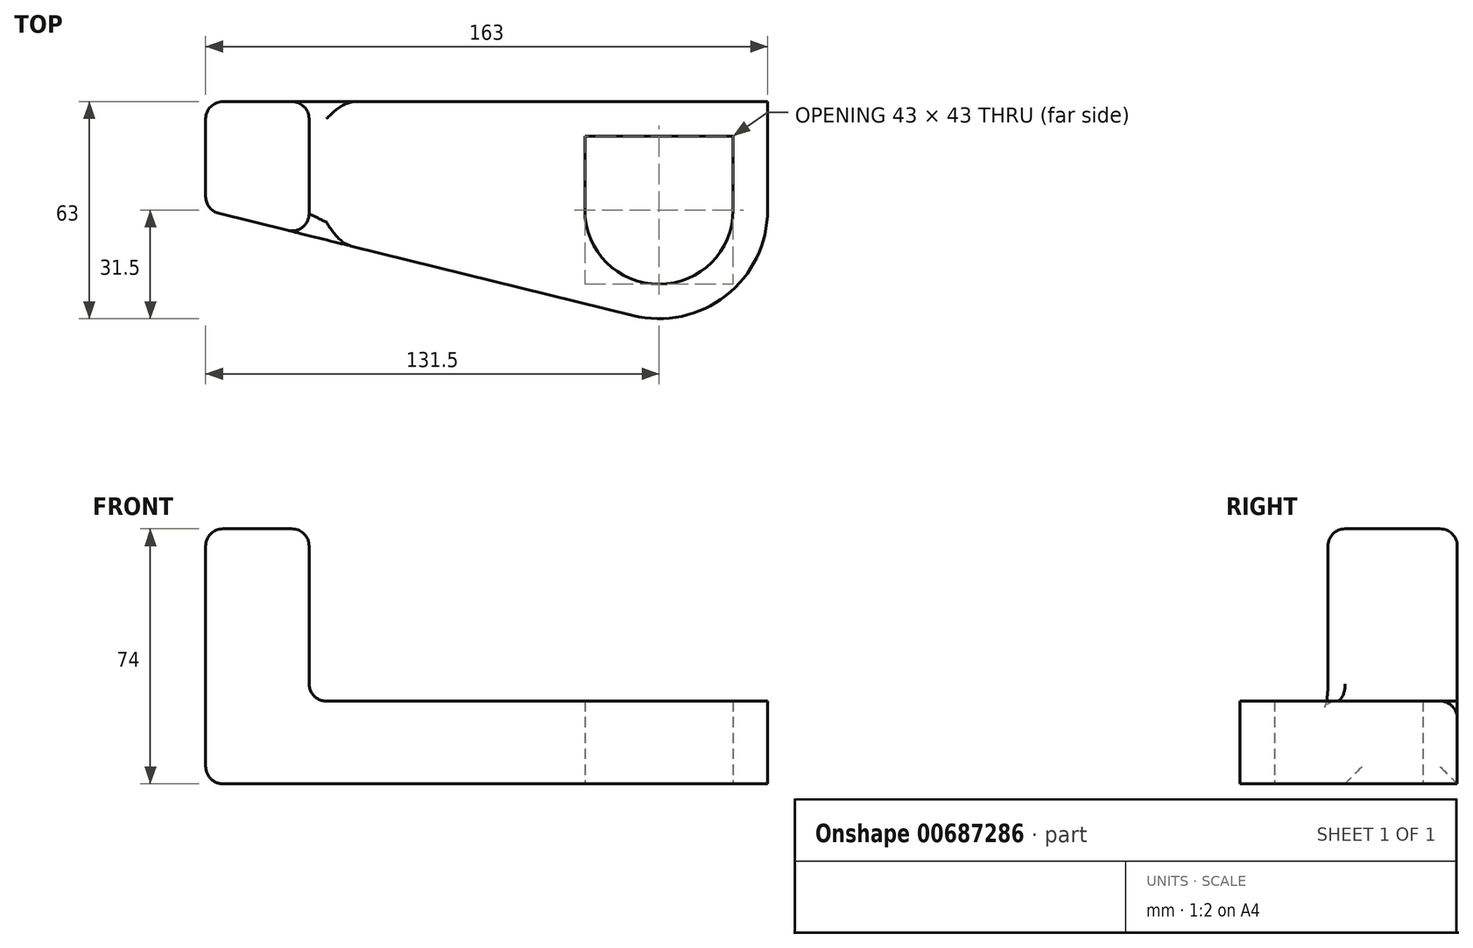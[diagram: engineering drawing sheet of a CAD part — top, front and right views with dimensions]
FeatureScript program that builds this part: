
annotation { "Feature Type Name" : "Feature", "Feature Type Description" : "" }
export const myFeature = defineFeature(function(context is Context, id is Id, definition is map)
    precondition{}
    {
        {
            var Q0;
            Q0=qCreatedBy(makeId("Top.planeOp"),FACE);
            var sketch = newSketch(context, id + "F0", { "sketchPlane" : qUnion([Q0])});
            skLineSegment(sketch, "E0.bottom", {"start": v(0, 0) * mm, "end": v(43, 0) * mm});
            skLineSegment(sketch, "E0.top", {"start": v(0, 21.5) * mm, "end": v(43, 21.5) * mm});
            skLineSegment(sketch, "E0.left", {"start": v(0, 0) * mm, "end": v(0, 21.5) * mm});
            skLineSegment(sketch, "E0.right", {"start": v(43, 0) * mm, "end": v(43, 21.5) * mm});
            skArc(sketch, "E1", {"start": v(0, 0) * mm, "mid": v(21.5, -21.5) * mm, "end": v(43, 0) * mm});
            skLineSegment(sketch, "E2.0", {"start": v(-10, 31.5) * mm, "end": v(53, 31.5) * mm});
            skLineSegment(sketch, "E2.1", {"start": v(-10, 0) * mm, "end": v(-10, 31.5) * mm});
            skArc(sketch, "E2.2", {"start": v(-10, 0) * mm, "mid": v(21.5, -31.5) * mm, "end": v(53, 0) * mm});
            skLineSegment(sketch, "E2.3", {"start": v(53, 0) * mm, "end": v(53, 31.5) * mm});
            skLineSegment(sketch, "E3", {"start": v(-10, 31.5) * mm, "end": v(-110, 31.5) * mm});
            skLineSegment(sketch, "E4", {"start": v(-110, 31.5) * mm, "end": v(-110, 0) * mm});
            skLineSegment(sketch, "E5", {"start": v(-110, 0) * mm, "end": v(13.95, -30.58) * mm});
            skSolve(sketch);
        }
        {
            var Q0;
            {var subQ1=sQuery(id+"F0.wireOp",EDGE,"E2.1");Q0=makeQuery(id+"F0.imprint","IMPRINT",FACE,{"disambiguationData":[TD([[makeQuery(id+"F0.imprint","IMPRINT",EDGE,{"derivedFrom":subQ1}),1.0]])]});}
            var Q1;
            Q1=makeQuery(id+"F0.imprint","IMPRINT",FACE,{"disambiguationData":[TD([[makeQuery(id+"F0.imprint","IMPRINT",EDGE,{"derivedFrom":sQuery(id+"F0.wireOp",EDGE,"E0.top")}),1.0]])]});
            extrude(context, id + "F1", {"entities" : qUnion([Q0, Q1]), "depth" : 24 * mm, "offsetDistance" : 25 * mm});
        }
        {
            var Q0;
            Q0=makeQuery(id+"F1.opExtrude","CAP_FACE",FACE,{"disambiguationData":[OSD([sQuery(id+"F0.wireOp",EDGE,"E0.top"),sQuery(id+"F0.wireOp",EDGE,"E0.left"),sQuery(id+"F0.wireOp",EDGE,"E0.right"),sQuery(id+"F0.wireOp",EDGE,"E1"),sQuery(id+"F0.wireOp",EDGE,"E2.0"),sQuery(id+"F0.wireOp",EDGE,"E2.2"),sQuery(id+"F0.wireOp",EDGE,"E2.3"),sQuery(id+"F0.wireOp",EDGE,"E3"),sQuery(id+"F0.wireOp",EDGE,"E4"),sQuery(id+"F0.wireOp",EDGE,"E5")])],"isStart":false});
            var sketch = newSketch(context, id + "F2", { "sketchPlane" : qUnion([Q0])});
            skLineSegment(sketch, "E6", {"start": v(-80, 31.5) * mm, "end": v(-80, -7.4) * mm});
            skLineSegment(sketch, "E7.0", {"start": v(53, 31.5) * mm, "end": v(-110, 31.5) * mm});
            skLineSegment(sketch, "E7.1", {"start": v(-110, 31.5) * mm, "end": v(-110, 0) * mm});
            skLineSegment(sketch, "E7.2", {"start": v(-110, 0) * mm, "end": v(13.95, -30.58) * mm});
            skArc(sketch, "E7.3", {"start": v(13.95, -30.58) * mm, "mid": v(40.92, -24.8) * mm, "end": v(53, 0) * mm});
            skLineSegment(sketch, "E7.4", {"start": v(53, 0) * mm, "end": v(53, 31.5) * mm});
            skLineSegment(sketch, "E7.5", {"start": v(0, 21.5) * mm, "end": v(43, 21.5) * mm});
            skLineSegment(sketch, "E7.6", {"start": v(0, 0) * mm, "end": v(0, 21.5) * mm});
            skArc(sketch, "E7.7", {"start": v(0, 0) * mm, "mid": v(21.5, -21.5) * mm, "end": v(43, 0) * mm});
            skLineSegment(sketch, "E7.8", {"start": v(43, 0) * mm, "end": v(43, 21.5) * mm});
            skSolve(sketch);
        }
        {
            var Q0;
            {var subQ0=sQuery(id+"F2.wireOp",EDGE,"E6");Q0=makeQuery(id+"F2.imprint","IMPRINT",FACE,{"disambiguationData":[TD([[makeQuery(id+"F2.imprint","IMPRINT",EDGE,{"derivedFrom":subQ0}),-1.0]])]});}
            extrude(context, id + "F3", {"entities" : qUnion([Q0]), "operationType" : NewBodyOperationType.ADD, "depth" : 50 * mm, "offsetDistance" : 25 * mm});
        }
        {
            var Q0;
            Q0=makeQuery(id+"F3.boolean.opBoolean","MERGE",EDGE,{"derivedFrom":[makeQuery(id+"F1.opExtrude","SWEPT_EDGE",EDGE,{"disambiguationData":[OSD([sQuery(id+"F0.wireOp",EDGE,"E3"),sQuery(id+"F0.wireOp",EDGE,"E4")])]}),makeQuery(id+"F3.opExtrude","SWEPT_EDGE",EDGE,{"disambiguationData":[OSD([sQuery(id+"F2.wireOp",EDGE,"E7.0"),sQuery(id+"F2.wireOp",EDGE,"E7.1")])]})]});
            var Q1;
            Q1=makeQuery(id+"F3.boolean.opBoolean","MERGE",FACE,{"derivedFrom":[makeQuery(id+"F1.opExtrude","SWEPT_FACE",FACE,{"disambiguationData":[OSD([sQuery(id+"F0.wireOp",EDGE,"E4")])]}),makeQuery(id+"F3.opExtrude","SWEPT_FACE",FACE,{"disambiguationData":[OSD([sQuery(id+"F2.wireOp",EDGE,"E7.1")])]})]});
            var Q2;
            Q2=makeQuery(id+"F3.opExtrude","CAP_FACE",FACE,{"disambiguationData":[OSD([sQuery(id+"F2.wireOp",EDGE,"E6"),sQuery(id+"F2.wireOp",EDGE,"E7.0"),sQuery(id+"F2.wireOp",EDGE,"E7.1"),sQuery(id+"F2.wireOp",EDGE,"E7.2")])],"isStart":false});
            var Q3;
            Q3=makeQuery(id+"F3.opExtrude","SWEPT_FACE",FACE,{"disambiguationData":[OSD([sQuery(id+"F2.wireOp",EDGE,"E6")])]});
            fillet(context, id + "F4", {"entities" : qUnion([Q0, Q1, Q2, Q3]), "radius" : 5 * mm, "tangentPropagation" : true, "allowEdgeOverflow" : false});
        }
    });
